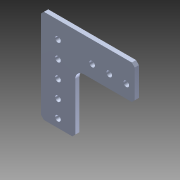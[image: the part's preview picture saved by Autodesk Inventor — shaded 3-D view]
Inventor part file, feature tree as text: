
AUTODESK INVENTOR PART (.ipt)
format: ipt  version: 2014 (Build 180170000, 170)  size: 183,808 bytes
history: native  units: in
note: dims shown in document units (in); Inventor stores cm internally (conversion verified against a paired STEP export)
features: extrude x3, sketch x3, other x2, imported_body x1
ambient origin geometry x8: Origin, YZ Plane, XZ Plane, XY Plane, X Axis, Y Axis, Z Axis, Center Point
bodies: Body1 (feature_tree)
feature tree (9):
  other  "Break-Corner1"
  other  "217-3548-STEP1"
  extrude  "Extrusion1"  Depth=1.75in
  extrude  "Extrusion2"  Depth=0.125in TaperAngle=0.0deg
  extrude  "Extrusion3"  Depth=0.3937in
  imported_body  "Base1"
  sketch  "Sketch1"  dims[d0=0.035in d1=0.0in d2=1.75in]
  sketch  "Sketch2"  dims[d3=1.0in d4=0.125in d5=0.0in]
  sketch  "Sketch3"  dims[d6=0.125in d8=1.1811in d10=0.5in d11=0.3937in d13=1.0in d15=0.125in d16=0.0in d17=1.0in]
